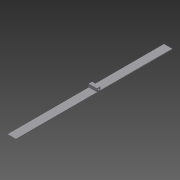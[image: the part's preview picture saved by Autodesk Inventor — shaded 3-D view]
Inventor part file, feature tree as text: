
AUTODESK INVENTOR PART (.ipt)
format: ipt  version: 2014 SP1 (Build 180222100, 222)  size: 91,648 bytes
history: native  units: mm
features: sketch x4, extrude x3, plane x1, projected_geometry x1
ambient origin geometry x8: Origin, YZ Plane, XZ Plane, XY Plane, X Axis, Y Axis, Z Axis, Center Point
bodies: Solid1 (feature_tree)
feature tree (9):
  extrude  "Extrusion1"  Depth=5.0mm
  plane  "Work Plane1"
  sketch  "Sketch3"  dims[d2=955.0mm d3=0.0mm d17=0.0mm]
  extrude  "Extrusion4"  TaperAngle=0.0deg  [1 undecoded]
  extrude  "Extrusion5"  Depth=20.0mm TaperAngle=0.0deg
  sketch  "Sketch1"  dims[d0=50.0mm d1=5.0mm]
  projected_geometry  "Projected Loop1"
  sketch  "Sketch5"  dims[d22=10.0mm d25=20.0mm d26=0.0mm]
  sketch  "Sketch6"  dims[d27=10.0mm d28=10.0mm d29=50.0mm d30=0.0mm]
note: 1 required parameter value undecoded (feature->parameter linkage not recoverable at this tier; creation-order binding heuristic only, values carry confidence <= 0.55)
